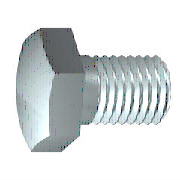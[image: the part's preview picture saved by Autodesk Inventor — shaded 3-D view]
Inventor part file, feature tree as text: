
AUTODESK INVENTOR PART (.ipt)
format: ipt  version: 2013 (Build 170138000, 138)  size: 186,880 bytes
history: native  units: mm (DEFAULTED — no unit token found)
features: sketch x2, extrude x1, chamfer x1, plane x1
ambient origin geometry x7: Origin, YZ Plane, XZ Plane, X Axis, Y Axis, Z Axis, Center Point
bodies: Solid1 (feature_tree), Body (feature_tree)
feature tree (5):
  extrude  "Head"  TaperAngle=90.0deg  [1 undecoded]
  chamfer  "Chamfer1"  [1 undecoded]
  plane  "Work Plane1"
  sketch  "Sketch1"  dims[d2=8.0mm d12=90.0deg]
  sketch  "Sketch2"  dims[d3=5.68mm d4=0.0mm d21=90.0deg d6=0.766813mm d7=0.766912mm d8=0.0mm d11=13.0mm d15=22.0mm d16=0.0mm d55=45.0deg d58=0.0mm d59=60.0mm d65=13.0mm d67=30.0deg d68=15.6mm d69=5.68mm d71=0.1mm d73=0.0mm]
note: 2 required parameter values undecoded (feature->parameter linkage not recoverable at this tier; creation-order binding heuristic only, values carry confidence <= 0.55)
